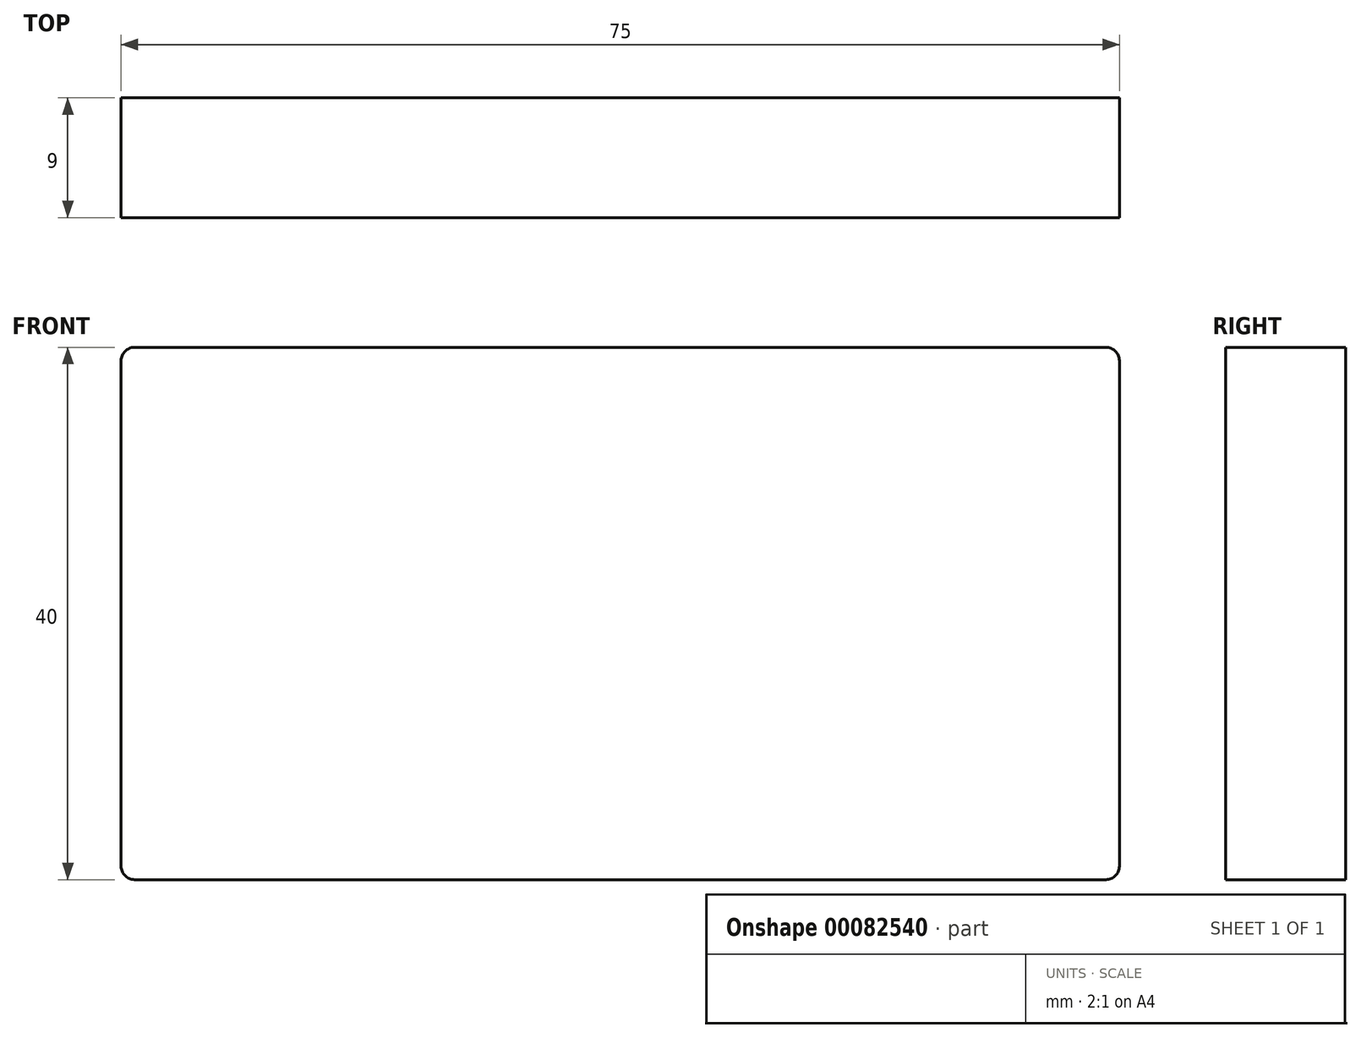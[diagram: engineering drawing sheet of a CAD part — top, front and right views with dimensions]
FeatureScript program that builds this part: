
annotation { "Feature Type Name" : "Feature", "Feature Type Description" : "" }
export const myFeature = defineFeature(function(context is Context, id is Id, definition is map)
    precondition{}
    {
        {
            var Q0;
            Q0=qCreatedBy(makeId("Front.planeOp"),FACE);
            var sketch = newSketch(context, id + "F0", { "sketchPlane" : qUnion([Q0])});
            skLineSegment(sketch, "E0", {"start": v(37.5, 20) * mm, "end": v(0, 20) * mm});
            skLineSegment(sketch, "E1", {"start": v(37.5, 20) * mm, "end": v(37.5, -20) * mm});
            skLineSegment(sketch, "E2", {"start": v(37.5, -20) * mm, "end": v(0, -20) * mm});
            skLineSegment(sketch, "E3.MirrorCS", {"start": v(-37.5, 20) * mm, "end": v(-37.5, -20) * mm});
            skLineSegment(sketch, "E4.MirrorCS", {"start": v(-37.5, -20) * mm, "end": v(0, -20) * mm});
            skLineSegment(sketch, "E5.MirrorCS", {"start": v(-37.5, 20) * mm, "end": v(0, 20) * mm});
            skSolve(sketch);
        }
        {
            var Q0;
            Q0=qSketchRegion(id+"F0",true);
            extrude(context, id + "F1", {"entities" : qUnion([Q0]), "depth" : 9 * mm});
        }
        {
            var Q0;
            Q0=makeQuery(id+"F1.opExtrude","SWEPT_EDGE",EDGE,{"disambiguationData":[OSD([sQuery(id+"F0.wireOp",EDGE,"E3.MirrorCS"),sQuery(id+"F0.wireOp",EDGE,"E5.MirrorCS")])]});
            var Q1;
            Q1=makeQuery(id+"F1.opExtrude","SWEPT_EDGE",EDGE,{"disambiguationData":[OSD([sQuery(id+"F0.wireOp",EDGE,"E3.MirrorCS"),sQuery(id+"F0.wireOp",EDGE,"E4.MirrorCS")])]});
            var Q2;
            Q2=makeQuery(id+"F1.opExtrude","SWEPT_EDGE",EDGE,{"disambiguationData":[OSD([sQuery(id+"F0.wireOp",EDGE,"E0"),sQuery(id+"F0.wireOp",EDGE,"E1")])]});
            var Q3;
            Q3=makeQuery(id+"F1.opExtrude","SWEPT_EDGE",EDGE,{"disambiguationData":[OSD([sQuery(id+"F0.wireOp",EDGE,"E1"),sQuery(id+"F0.wireOp",EDGE,"E2")])]});
            fillet(context, id + "F2", {"entities" : qUnion([Q0, Q1, Q2, Q3]), "radius" : 1 * mm, "tangentPropagation" : true, "allowEdgeOverflow" : false});
        }
    });
